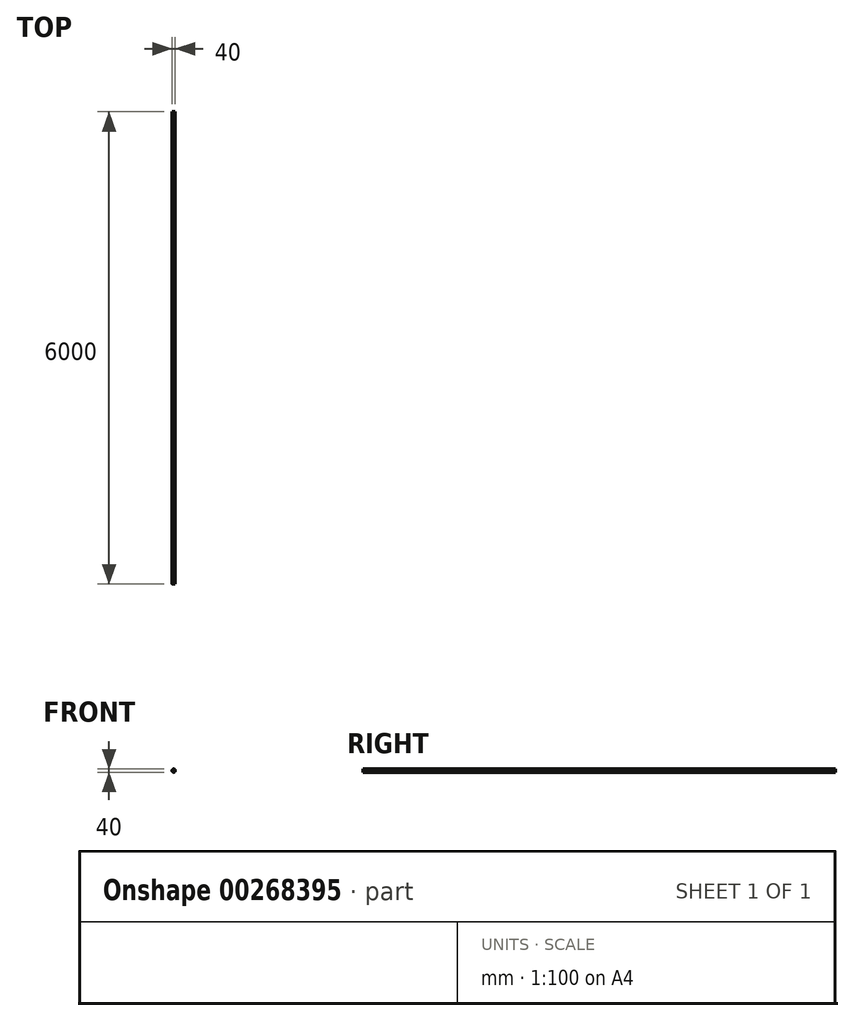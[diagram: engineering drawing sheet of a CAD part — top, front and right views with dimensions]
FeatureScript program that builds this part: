
annotation { "Feature Type Name" : "Feature", "Feature Type Description" : "" }
export const myFeature = defineFeature(function(context is Context, id is Id, definition is map)
    precondition{}
    {
        {
            var Q0;
            Q0=qCreatedBy(makeId("Front.planeOp"),FACE);
            var sketch = newSketch(context, id + "F0", { "sketchPlane" : qUnion([Q0])});
            skCircle(sketch, "E0", {"center": v(0, 0) * mm, "radius": 20 * mm});
            skSolve(sketch);
        }
        {
            var Q0;
            Q0=makeQuery(id+"F0.imprint","IMPRINT",FACE,{"disambiguationData":[TD([[makeQuery(id+"F0.imprint","IMPRINT",EDGE,{"derivedFrom":sQuery(id+"F0.wireOp",EDGE,"E0")}),1.0]])]});
            extrude(context, id + "F1", {"entities" : qUnion([Q0]), "oppositeDirection" : true, "depth" : 6000 * mm, "offsetDistance" : 25 * mm});
        }
    });
